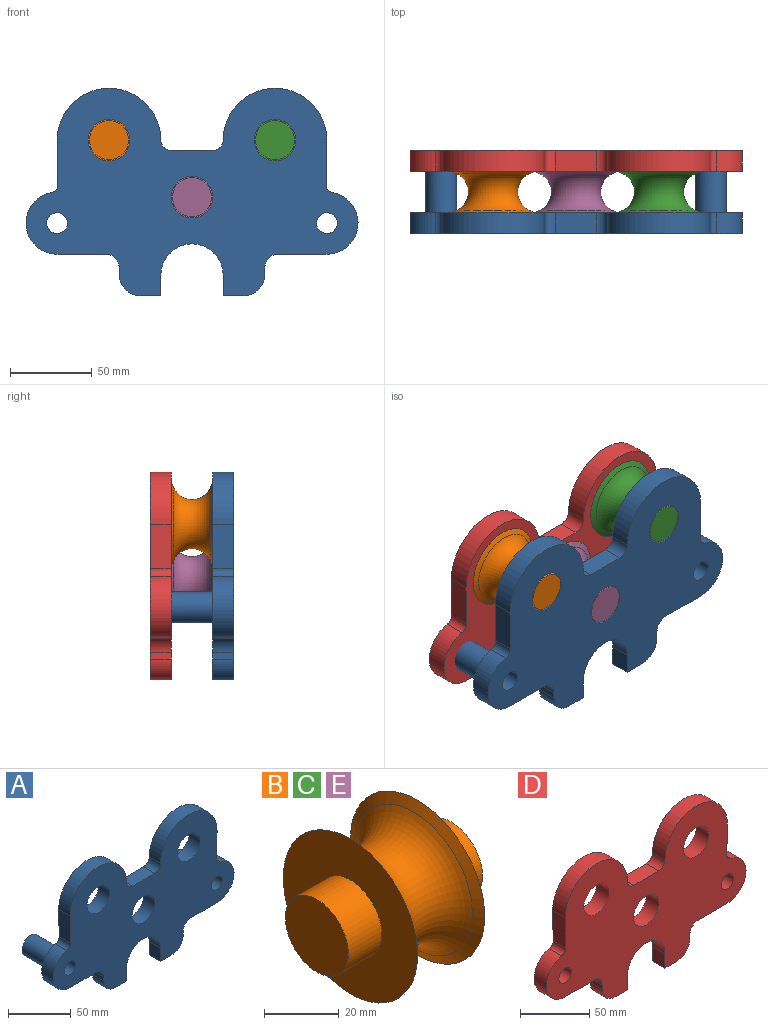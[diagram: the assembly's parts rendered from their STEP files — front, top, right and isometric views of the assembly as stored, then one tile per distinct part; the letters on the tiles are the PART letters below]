
ASSEMBLY  parts=5 mates=6
PART A: 35 faces, bbox 203.2x44.5x127 mm
  f0: plane 31.34x12.7mm, normal (0,0,-1), area 398.1mm2, adj f1,f19,f23,f24
  f1: cylinder r=19.05mm len=37.79mm, axis (0,1,0), area 723.2mm2, adj f0,f23,f24,f27
  f2: plane 27.3x12.7mm, normal (1,0,-0.02), area 346.7mm2, adj f3,f23,f24,f27
  f3: cylinder r=31.75mm len=63.5mm, axis (0,1,0), area 1266.8mm2, adj f2,f23,f24,f29
  f4: plane 25.4x12.7mm, normal (0,0,1), area 322.6mm2, adj f23,f24,f29,f30
  f5: cylinder r=31.75mm len=63.5mm, axis (0,1,0), area 1266.8mm2, adj f6,f23,f24,f30
  f6: plane 27.3x12.7mm, normal (-1,0,-0.02), area 346.7mm2, adj f5,f23,f24,f28
  f7: cylinder r=19.05mm len=37.79mm, axis (0,1,0), area 723.2mm2, adj f8,f23,f24,f28
  f8: plane 31.34x12.7mm, normal (0,0,-1), area 398.1mm2, adj f7,f9,f23,f24
  f9: cylinder r=9.53mm len=12.7mm, axis (0,1,0), area 147mm2, adj f8,f10,f23,f24
  f10: plane 12.7x3.78mm, normal (-1,0,0), area 48mm2, adj f9,f23,f24,f25
  f11: plane 12.7x12.7mm, normal (0,0,-1), area 161.3mm2, adj f12,f23,f24,f25
  f12: plane 12.7x12.7mm, normal (1,0,0), area 161.3mm2, adj f11,f13,f23,f24
  f13: cylinder r=19.05mm len=38.1mm, axis (0,1,0), area 760.1mm2, adj f12,f14,f23,f24
  f14: plane 12.7x12.7mm, normal (-1,0,0), area 161.3mm2, adj f13,f15,f23,f24
  f15: plane 12.7x12.7mm, normal (0,0,-1), area 161.3mm2, adj f14,f23,f24,f26
  f16: plane 12.7x3.78mm, normal (1,0,0), area 48mm2, adj f19,f23,f24,f26
  f17: cylinder r=6.35mm len=44.45mm, axis (0,1,0), area 1773.5mm2, adj f23,f32
  f18: cylinder r=12.7mm len=25.4mm, axis (0,1,0), area 1013.4mm2, adj f23,f24
  f19: cylinder r=9.53mm len=12.7mm, axis (0,1,0), area 147mm2, adj f0,f16,f23,f24
  f20: cylinder r=12.7mm len=25.4mm, axis (0,1,0), area 1013.4mm2, adj f23,f24
  f21: cylinder r=12.7mm len=25.4mm, axis (0,1,0), area 1013.4mm2, adj f23,f24
  f22: cylinder r=6.35mm len=44.45mm, axis (0,1,0), area 1773.5mm2, adj f23,f34
  f23: plane 203.2x127mm, normal (0,-1,0), area 14996mm2, adj f0,f1,f2,f3,f4,f5,f6,f7
  f24: plane 203.2x127mm, normal (0,1,0), area 14679.3mm2, adj f0,f1,f2,f3,f4,f5,f6,f7
  f25: cylinder r=12.7mm len=12.7mm, axis (0,1,0), area 253.4mm2, adj f10,f11,f23,f24
  f26: cylinder r=12.7mm len=12.7mm, axis (0,1,0), area 253.4mm2, adj f15,f16,f23,f24
  f27: cylinder r=4.76mm len=12.7mm, axis (0,1,0), area 85.1mm2, adj f1,f2,f23,f24
  f28: cylinder r=4.76mm len=12.7mm, axis (0,1,0), area 85.1mm2, adj f6,f7,f23,f24
  f29: cylinder r=6.35mm len=12.7mm, axis (0,1,0), area 126.7mm2, adj f3,f4,f23,f24
  f30: cylinder r=6.35mm len=12.7mm, axis (0,-1,0), area 126.7mm2, adj f4,f5,f23,f24
  f31: cylinder r=9.53mm len=31.75mm, axis (0,-1,0), area 1900.2mm2, adj f24,f32
  f32: plane 19.05x19.05mm, normal (0,1,0), area 158.3mm2, adj f17,f31
  f33: cylinder r=9.53mm len=31.75mm, axis (0,-1,0), area 1900.2mm2, adj f24,f34
  f34: plane 19.05x19.05mm, normal (0,1,0), area 158.3mm2, adj f22,f33
PART B: 9 faces, bbox 50.8x59.4x59.4 mm
  f0: cylinder r=11.91mm len=23.83mm, axis (-1,0,0), area 950.6mm2, adj f1,f8
  f1: plane 23.83x23.83mm, normal (-1,0,0), area 445.8mm2, adj f0
  f2: plane 23.83x23.83mm, normal (1,0,0), area 445.8mm2, adj f3
  f3: cylinder r=11.91mm len=23.83mm, axis (-1,0,0), area 950.6mm2, adj f2,f4
  f4: plane 50.8x50.8mm, normal (1,0,0), area 1581mm2, adj f3,f5
  f5: cone r=25.4mm half-angle=65deg, axis (1,0,0), area 524.1mm2, adj f4,f6
  f6: torus R=27.46mm, axis (-1,0,0), area 3100.2mm2, adj f5,f7
  f7: cone r=25.4mm half-angle=65deg, axis (-1,0,0), area 524.1mm2, adj f6,f8
  f8: plane 50.8x50.8mm, normal (-1,0,0), area 1581mm2, adj f0,f7
PART C: same geometry as B
PART D: 31 faces, bbox 203.2x12.7x127 mm
  f0: plane 31.34x12.7mm, normal (0,0,-1), area 398.1mm2, adj f1,f19,f23,f24
  f1: cylinder r=19.05mm len=37.79mm, axis (0,1,0), area 723.2mm2, adj f0,f23,f24,f27
  f2: plane 27.3x12.7mm, normal (1,0,-0.02), area 346.7mm2, adj f3,f23,f24,f27
  f3: cylinder r=31.75mm len=63.5mm, axis (0,1,0), area 1266.8mm2, adj f2,f23,f24,f29
  f4: plane 25.4x12.7mm, normal (0,0,1), area 322.6mm2, adj f23,f24,f29,f30
  f5: cylinder r=31.75mm len=63.5mm, axis (0,1,0), area 1266.8mm2, adj f6,f23,f24,f30
  f6: plane 27.3x12.7mm, normal (-1,0,-0.02), area 346.7mm2, adj f5,f23,f24,f28
  f7: cylinder r=19.05mm len=37.79mm, axis (0,1,0), area 723.2mm2, adj f8,f23,f24,f28
  f8: plane 31.34x12.7mm, normal (0,0,-1), area 398.1mm2, adj f7,f9,f23,f24
  f9: cylinder r=9.53mm len=12.7mm, axis (0,1,0), area 147mm2, adj f8,f10,f23,f24
  f10: plane 12.7x3.78mm, normal (-1,0,0), area 48mm2, adj f9,f23,f24,f25
  f11: plane 12.7x12.7mm, normal (0,0,-1), area 161.3mm2, adj f12,f23,f24,f25
  f12: plane 12.7x12.7mm, normal (1,0,0), area 161.3mm2, adj f11,f13,f23,f24
  f13: cylinder r=19.05mm len=38.1mm, axis (0,1,0), area 760.1mm2, adj f12,f14,f23,f24
  f14: plane 12.7x12.7mm, normal (-1,0,0), area 161.3mm2, adj f13,f15,f23,f24
  f15: plane 12.7x12.7mm, normal (0,0,-1), area 161.3mm2, adj f14,f23,f24,f26
  f16: plane 12.7x3.78mm, normal (1,0,0), area 48mm2, adj f19,f23,f24,f26
  f17: cylinder r=6.35mm len=12.7mm, axis (0,1,0), area 506.7mm2, adj f23,f24
  f18: cylinder r=12.7mm len=25.4mm, axis (0,1,0), area 1013.4mm2, adj f23,f24
  f19: cylinder r=9.53mm len=12.7mm, axis (0,1,0), area 147mm2, adj f0,f16,f23,f24
  f20: cylinder r=12.7mm len=25.4mm, axis (0,1,0), area 1013.4mm2, adj f23,f24
  f21: cylinder r=12.7mm len=25.4mm, axis (0,1,0), area 1013.4mm2, adj f23,f24
  f22: cylinder r=6.35mm len=12.7mm, axis (0,1,0), area 506.7mm2, adj f23,f24
  f23: plane 203.2x127mm, normal (0,-1,0), area 14996mm2, adj f0,f1,f2,f3,f4,f5,f6,f7
  f24: plane 203.2x127mm, normal (0,1,0), area 14996mm2, adj f0,f1,f2,f3,f4,f5,f6,f7
  f25: cylinder r=12.7mm len=12.7mm, axis (0,1,0), area 253.4mm2, adj f10,f11,f23,f24
  f26: cylinder r=12.7mm len=12.7mm, axis (0,1,0), area 253.4mm2, adj f15,f16,f23,f24
  f27: cylinder r=4.76mm len=12.7mm, axis (0,1,0), area 85.1mm2, adj f1,f2,f23,f24
  f28: cylinder r=4.76mm len=12.7mm, axis (0,1,0), area 85.1mm2, adj f6,f7,f23,f24
  f29: cylinder r=6.35mm len=12.7mm, axis (0,1,0), area 126.7mm2, adj f3,f4,f23,f24
  f30: cylinder r=6.35mm len=12.7mm, axis (0,-1,0), area 126.7mm2, adj f4,f5,f23,f24
PART E: same geometry as B
PLACE A t=(-0.39,-15.67,-2.53)mm fixed
PLACE B rot(axis=(-0.58,0.58,-0.58),120deg) t=(-51.19,3.38,32.39)mm
PLACE C rot(axis=(-0.58,0.58,-0.58),120deg) t=(50.41,3.38,32.39)mm
PLACE D t=(-0.39,22.43,-2.53)mm
PLACE E rot(axis=(-0.58,0.58,-0.58),120deg) t=(-0.39,3.38,-2.53)mm
MATE revolute C.f0 <-> A.f3  axis (0,-1,0) through (50.41,-22.02,32.39)mm
MATE revolute B.f0 <-> A.f5  axis (0,-1,0) through (-51.19,-22.02,32.39)mm
MATE revolute E.f0 <-> A.f20  axis (0,-1,0) through (-0.39,-22.02,-2.53)mm
MATE revolute D.f20 <-> E.f0  axis (0,1,0) through (-0.39,28.78,-2.53)mm
MATE revolute D.f5 <-> B.f0  axis (0,1,0) through (-51.19,28.78,32.39)mm
MATE revolute D.f3 <-> C.f0  axis (0,1,0) through (50.41,28.78,32.39)mm
